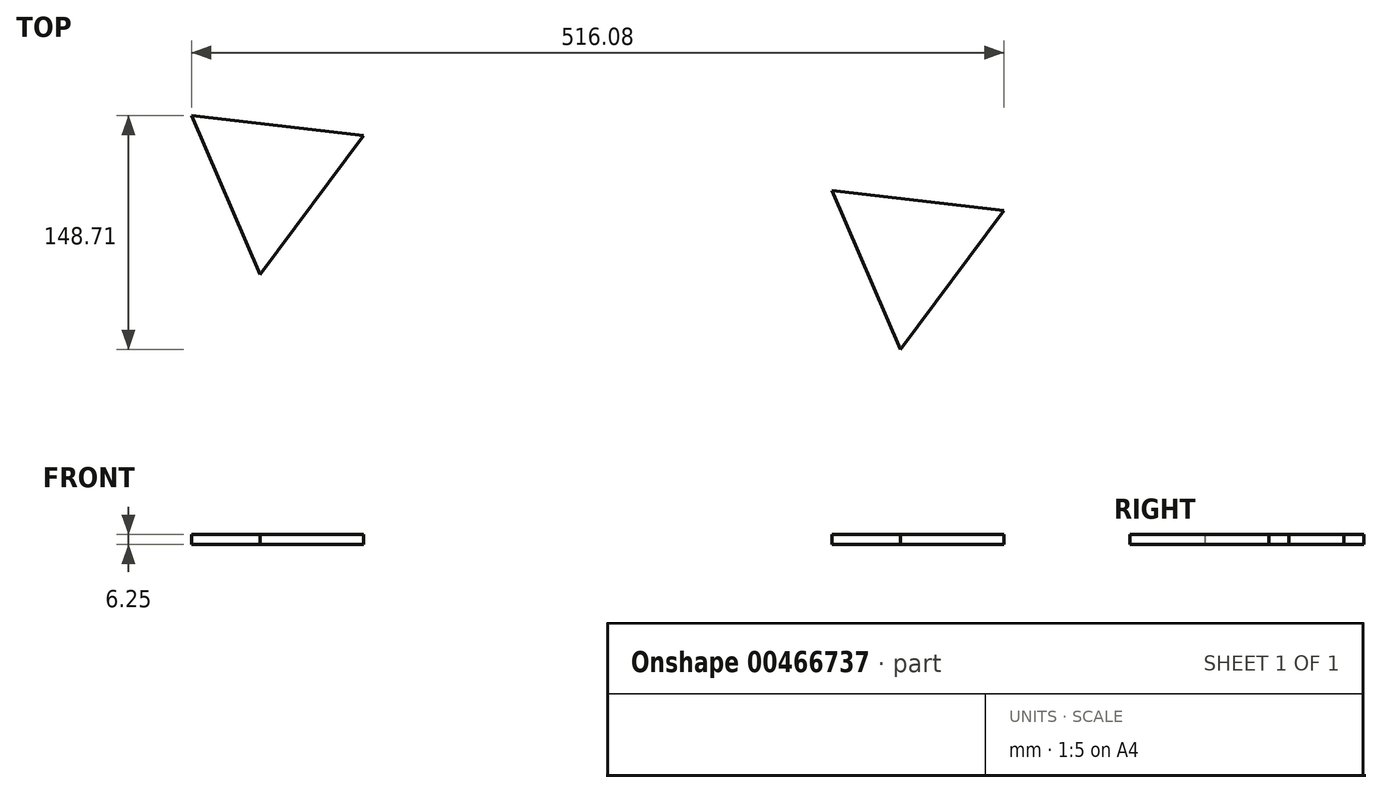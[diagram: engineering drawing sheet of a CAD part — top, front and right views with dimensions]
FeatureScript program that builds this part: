
annotation { "Feature Type Name" : "Feature", "Feature Type Description" : "" }
export const myFeature = defineFeature(function(context is Context, id is Id, definition is map)
    precondition{}
    {
        {
            var Q0;
            Q0=qCreatedBy(makeId("Top.planeOp"),FACE);
            var sketch = newSketch(context, id + "F0", { "sketchPlane" : qUnion([Q0])});
            skCircle(sketch, "E0.cCircle", {"center": v(0, 0) * mm, "radius": 150 * mm, "construction": true});
            skLineSegment(sketch, "E0.0", {"start": v(275.5, 118.73) * mm, "end": v(-34.93, -297.96) * mm});
            skLineSegment(sketch, "E0.1", {"start": v(-34.93, -297.96) * mm, "end": v(-240.57, 179.23) * mm});
            skLineSegment(sketch, "E0.2", {"start": v(-240.57, 179.23) * mm, "end": v(275.5, 118.73) * mm});
            skPoint(sketch, "E0.0.midPoint", {"position": v(120.29, -89.62) * mm});
            skLineSegment(sketch, "E1", {"start": v(-197.04, 78.21) * mm, "end": v(-131.32, 166.42) * mm});
            skLineSegment(sketch, "E2", {"start": v(-131.32, 166.42) * mm, "end": v(-240.57, 179.23) * mm});
            skLineSegment(sketch, "E3", {"start": v(-34.93, -297.96) * mm, "end": v(-78.47, -196.94) * mm});
            skLineSegment(sketch, "E4", {"start": v(-78.47, -196.94) * mm, "end": v(30.79, -209.75) * mm});
            skLineSegment(sketch, "E5", {"start": v(30.79, -209.75) * mm, "end": v(-34.93, -297.96) * mm});
            skLineSegment(sketch, "E6", {"start": v(275.5, 118.73) * mm, "end": v(166.26, 131.54) * mm});
            skLineSegment(sketch, "E7", {"start": v(166.26, 131.54) * mm, "end": v(209.79, 30.52) * mm});
            skLineSegment(sketch, "E8", {"start": v(209.79, 30.52) * mm, "end": v(275.5, 118.73) * mm});
            skLineSegment(sketch, "E9", {"start": v(-197.04, 78.21) * mm, "end": v(-78.47, -196.94) * mm});
            skLineSegment(sketch, "E10", {"start": v(-197.04, 78.21) * mm, "end": v(-240.57, 179.23) * mm});
            skLineSegment(sketch, "E11", {"start": v(30.79, -209.75) * mm, "end": v(209.79, 30.52) * mm});
            skSolve(sketch);
        }
        {
            var Q0;
            Q0=makeQuery(id+"F0.imprint","IMPRINT",FACE,{"disambiguationData":[TD([[makeQuery(id+"F0.imprint","IMPRINT",EDGE,{"derivedFrom":sQuery(id+"F0.wireOp",EDGE,"E0.2")}),-1.0]])]});
            extrude(context, id + "F1", {"entities" : qUnion([Q0]), "depth" : 6.25 * mm});
        }
    });
